# Revit family: P5500T_Column
name_source: partatom
category: Structural Columns
units: mm (PartAtom-declared; Revit-internal decimal feet)

## family parameters
Always export as geometry = No
Beam cutback in plan = From bounding box
Cut with Voids When Loaded = No
Material for Model Behavior = Other
OmniClass Number = 23.25.30.11.14.11
OmniClass Title = Columns
Section Shape = Not Defined
Shared = Yes
Show family pre-cut in plan views = Yes

## types (6) — shared parameters
Assembly Code = B10
Description = P5500T - Column - 1-5/8" x 2 7/16", 12 Gauge, Slotted
Height = 2.438 "
Manufacturer = Atkore Unistrut
Model = P5500T
Salsify ID1 = US-P5500T
URL = https://www.atkore.com

## per-type parameters (varying)
| type | Power-Strut Part Number | Structural Material | UPC-10ft | UPC-20ft | Unit Weight |
| P5500T SS |  | Stainless Steel | "0" | "0" | 2.47 lb/ft |
| P5500T GR |  | Green | "786364041179" | "786364041216" | 2.47 lb/ft |
| P5500T ZD |  | Zinc Dichromate | "786364055305" | "0" | 2.47 lb/ft |
| P5500T HG |  | Hot Dip Galvanized | "786364041186" | "786364041223" | 2.47 lb/ft |
| P5500T PL |  | Plain | "786364041209" | "786364041247" | 2.42 lb/ft |
| P5500T PG | PS 150 EH PGAL | Pre-Galvanized | "0786364041193" | "0786364041230" | 2.47 lb/ft |

note: column(s) folded — value = type name in every type: Part Number

## geometry (parser evidence)
native form markers: Sweep x9
no freeform markers — native parametric forms only
